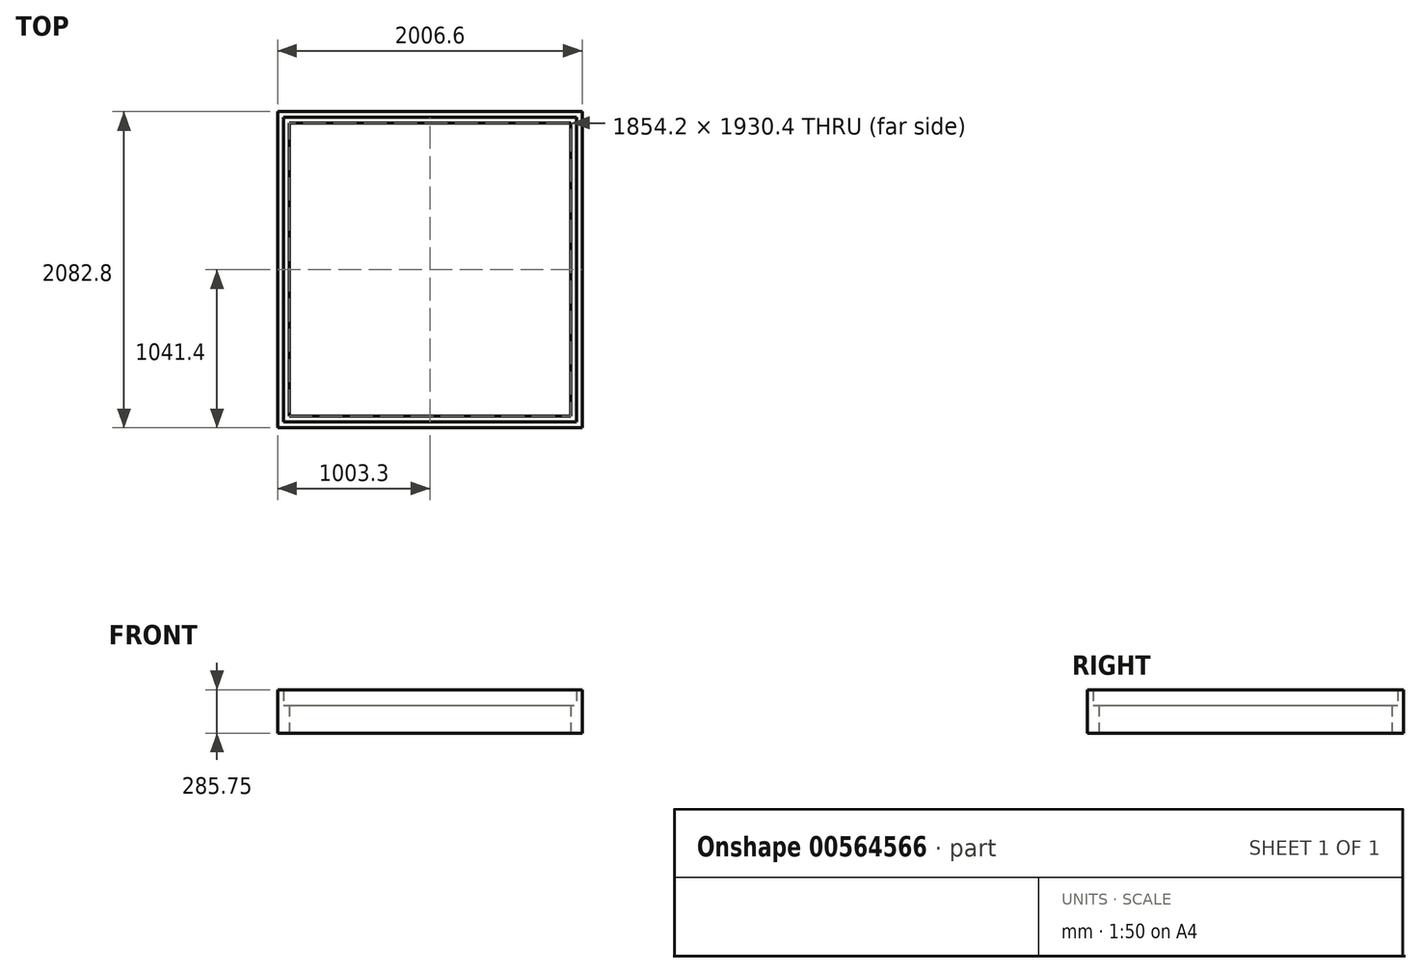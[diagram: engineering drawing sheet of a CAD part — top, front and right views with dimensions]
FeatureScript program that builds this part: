
annotation { "Feature Type Name" : "Feature", "Feature Type Description" : "" }
export const myFeature = defineFeature(function(context is Context, id is Id, definition is map)
    precondition{}
    {
        {
            var Q0;
            Q0=qCreatedBy(makeId("Top.planeOp"),FACE);
            var sketch = newSketch(context, id + "F0", { "sketchPlane" : qUnion([Q0])});
            skLineSegment(sketch, "E0.bottom", {"start": v(-1264.2, -960.86) * mm, "end": v(666.2, -960.86) * mm});
            skLineSegment(sketch, "E0.top", {"start": v(-1264.2, 1045.74) * mm, "end": v(666.2, 1045.74) * mm});
            skLineSegment(sketch, "E0.left", {"start": v(-1264.2, -960.86) * mm, "end": v(-1264.2, 1045.74) * mm});
            skLineSegment(sketch, "E0.right", {"start": v(666.2, -960.86) * mm, "end": v(666.2, 1045.74) * mm});
            skLineSegment(sketch, "E1.0", {"start": v(-1226.1, -922.76) * mm, "end": v(-1226.1, 1007.64) * mm});
            skLineSegment(sketch, "E1.1", {"start": v(-1226.1, -922.76) * mm, "end": v(628.1, -922.76) * mm});
            skLineSegment(sketch, "E1.2", {"start": v(628.1, -922.76) * mm, "end": v(628.1, 1007.64) * mm});
            skLineSegment(sketch, "E1.3", {"start": v(-1226.1, 1007.64) * mm, "end": v(628.1, 1007.64) * mm});
            skLineSegment(sketch, "E2.0", {"start": v(-1302.3, -998.96) * mm, "end": v(704.3, -998.96) * mm});
            skLineSegment(sketch, "E2.1", {"start": v(-1302.3, -998.96) * mm, "end": v(-1302.3, 1083.84) * mm});
            skLineSegment(sketch, "E2.2", {"start": v(-1302.3, 1083.84) * mm, "end": v(704.3, 1083.84) * mm});
            skLineSegment(sketch, "E2.3", {"start": v(704.3, -998.96) * mm, "end": v(704.3, 1083.84) * mm});
            skSolve(sketch);
        }
        {
            var Q0;
            Q0=makeQuery(id+"F0.imprint","IMPRINT",FACE,{"disambiguationData":[TD([[makeQuery(id+"F0.imprint","IMPRINT",EDGE,{"derivedFrom":sQuery(id+"F0.wireOp",EDGE,"E0.bottom")}),1.0]])]});
            extrude(context, id + "F1", {"entities" : qUnion([Q0]), "depth" : 184.15 * mm, "offsetDistance" : 25.4 * mm});
        }
        {
            var Q0;
            Q0 = qSketchRegion(id + "F0", true);
            extrude(context, id + "F2", {"entities" : qUnion([Q0]), "operationType" : NewBodyOperationType.ADD, "depth" : 285.75 * mm, "offsetDistance" : 25.4 * mm});
        }
    });
